# Revit family: Valve-Float-Cla_Val-624_01-Ductile_Iron-Flanged-SI--
name_source: partatom
category: Pipe Accessories
units: mm (PartAtom-declared; Revit-internal decimal feet)

## family parameters
Always vertical = Yes
Cut with Voids When Loaded = No
Part Type = Valve - Breaks Into
Round Connector Dimension = Use Diameter
Shared = No
Work Plane-Based = No

## types (1)
- ERROR_LOAD TYPE CATALOG
    Assembly Code = D2090
    Body Material = Metal - CLA-VAL - Ductile Iron - Blue
    CV (liters per second) = 7.3
    Connection Axis to Valve Top = 178 mm
    Connection End Length = 17 mm
    Connection Radius = 40 mm
    Connection Size = 80 mm
    Connection Type = Flanged
    Connection to Connection = 260 mm
    Control Tube Line Size Diameter = 13 mm
    Control Tube Line Size Radius = 6 mm
    Cover Port Center Offset = 30 mm
    Cover Upper Flange Diameter = 168 mm
    Default Elevation = 0 mm
    Description = Float Valve
    ENGworks Global = http://www.ENGworksGlobal.com
    Flange Outside Radius = 95 mm
    Flow Configuration = In/Out
    K Coefficient = 6
    K Coefficient Table = Globe Valve Flanged
    Loss Method = K Coefficient
    Manufacturer = Cla-Val
    Maximum Flow Rate = 16.4 L/s
    Maximum Flow Rate Value = 16.4
    Maximum Operating Temperature = 82 °C
    Maximum Working Pressure = 17 bar
    Minimum Flow Rate = 0.0 L/s
    Minimum Flow Rate Value = 0
    Minimum Operating Temperature = -40 °C
    Model = 624-01
    Pilot Line Angle Offset = 77 mm
    Pilot Line Height Offset = 27 mm
    Pilot System Offset = 114 mm
    Pipe Plug Circumscribe Length = 13 mm
    Product Page URL = https://www.cla-val.com
    Series = Float Valve
    Side Port Outside Diameter = 40 mm
    Side Ports Offset from Flange = 54 mm
    Standards = ASTM A536 B16.42
    Tick Size = 150 mm
    URL = https://www.cla-val.com
    Unit Weight = 20 kgf
    Version = 1
    X Pilot System Offset = 330 mm
    Y Pilot System Offset = 254 mm
    Z Pilot System Offset = 254 mm

## geometry (parser evidence)
native form markers: Sweep x7
no freeform markers — native parametric forms only
